# Revit family: ElectricalEquipment_Hager_Klik7Pin_OccupancySensor
name_source: partatom
category: Lighting Devices
revit_build: Autodesk Revit 2015 (Build: 20160512_1515(x64)
units: mm (PartAtom-declared; Revit-internal decimal feet)

## types (1)
- KLIK Occupancy Sensor LDS PIR Pre-wired 3M
    Apparent Load = 0 VA
    Body Depth = 70 mm
    Body Diameter = 56 mm  [stored 0.183727 ft]
    Body Radius = 28 mm  [stored 0.0918635 ft]
    Breaking Capacity = 16A 250V AC1
    CE Approval = Yes
    Cover Diameter = 80 mm  [stored 0.262467 ft]
    Cover Height = 10 mm  [stored 0.0328084 ft]
    Cover Material = Default
    Cover Radius = 40 mm  [stored 0.131234 ft]
    Default Elevation = 1200 mm
    Description = KLIK Occupancy Sensor LDS PIR Pre-wired 3M
    Design Country = China
    Detection Angle = 360˚
    EAN = 3250617579100
    Enclosure = PC/ABS (V0)
    Enclosure Colour = White
    Enclosure Rating = IP41 / IK03
    Floor Detection Diameter = 7000 mm
    Frequency = 50 Hz
    Hager Catalogue Ref = EEK513W
    Height 1 = 3 mm  [stored 0.00984252 ft]
    Lens Material = Default
    Load Classification = Other
    Location of Manufacturer = Telford, TF1 7FT
    Manufacturer = Hager UK Ltd
    Manufacturer Country = United Kingdom
    Manufacturer Website = www.hager.co.uk
    Material = <By Category>
    Model = EEK513W
    Mounting = Ceiling
    Product Description = KLIK Occupancy Sensor LDS PIR Pre-wired 3M
    Product Family = Klik Lighting Occupancy Sensor
    Product Group = Klik
    Product Literature = http://www.hager.co.uk
    Product Range = Klik LDS
    Product URL = http://www.hager.co.uk
    Product Weight = 0.66 kg
    Radius 1 = 10 mm  [stored 0.0328084 ft]
    Reference Standard = IEC 60669-1
    Revision = 1
    Sensor Number of Poles = 1
    Sensor Voltage = 230 V
    Shape = Circular
    Technical Description = Used with KLDS** Marshalling Boxes
    Time Delayed Range = 1 to 60 minutes
    Type = Occupancy Sensor
    Type Comments = Used with KLDS** Marshalling Boxes
    URL = www.hager.co.uk
    Voltage = 230 V
    Warranty ID = Product Lifetime

note: [stored X ft] marks values corroborated as IEEE doubles in the binary element streams (Revit-internal decimal feet)

## geometry (parser evidence)
native form markers: Blend x2, Sweep x3
no freeform markers — native parametric forms only
